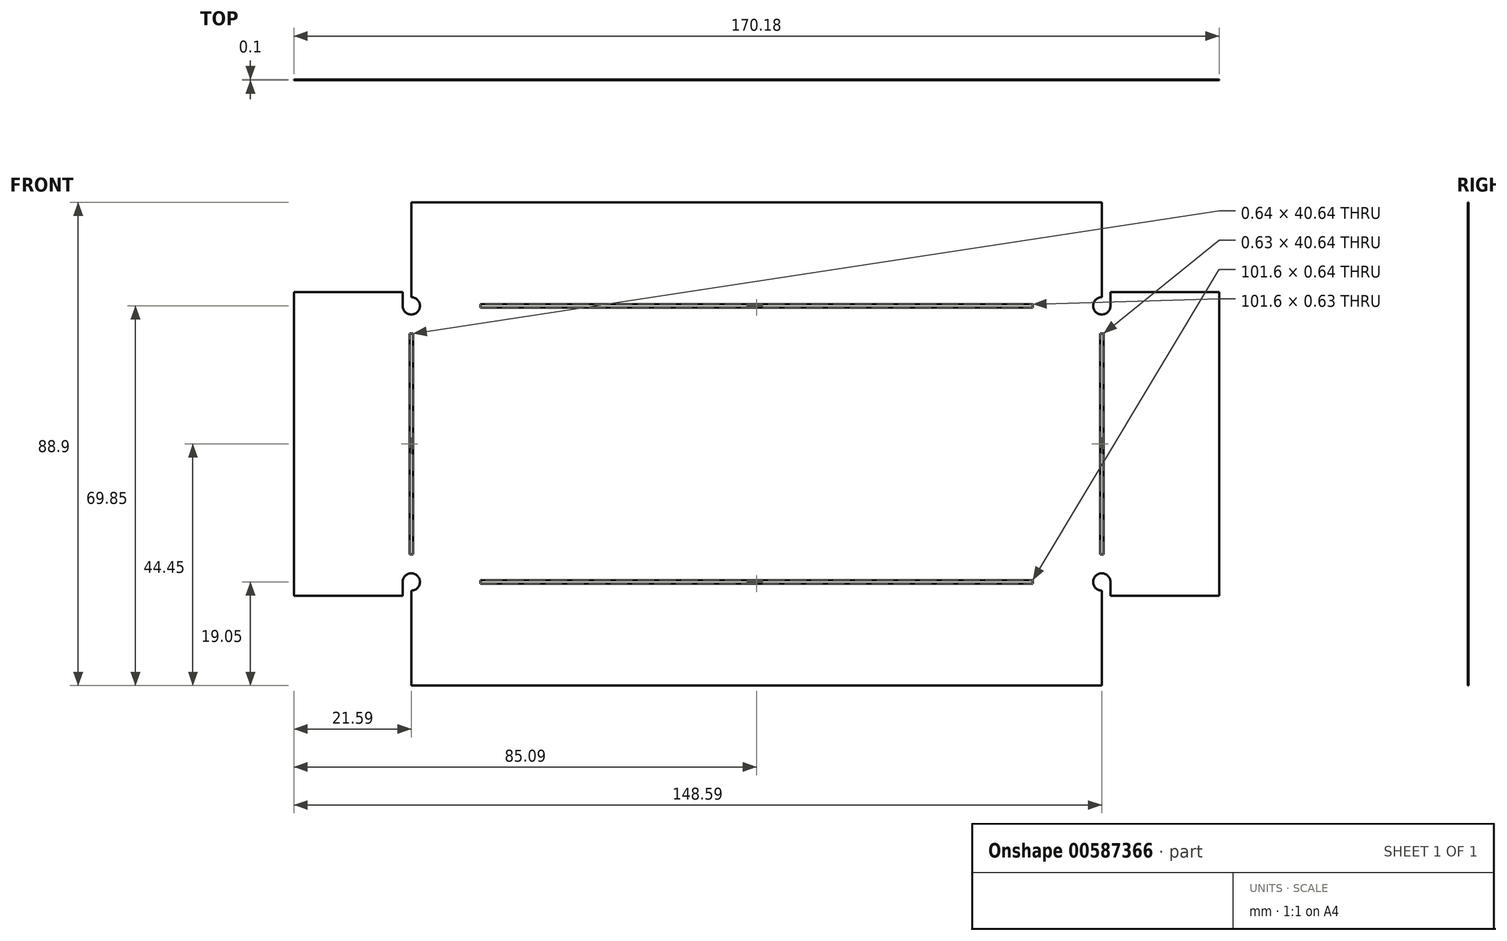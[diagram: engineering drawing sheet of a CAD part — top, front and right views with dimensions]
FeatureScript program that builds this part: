
annotation { "Feature Type Name" : "Feature", "Feature Type Description" : "" }
export const myFeature = defineFeature(function(context is Context, id is Id, definition is map)
    precondition{}
    {
        {
            assignVariable(context, id + "F0", {"name" : "matthick", "anyValue" : .1});
        }
        {
            var Q0;
            Q0=qCreatedBy(makeId("Front.planeOp"),FACE);
            var sketch = newSketch(context, id + "F1", { "sketchPlane" : qUnion([Q0])});
            skLineSegment(sketch, "E0.bottom", {"start": v(0, 0) * mm, "end": v(127, 0) * mm});
            skLineSegment(sketch, "E0.top", {"start": v(0, 50.8) * mm, "end": v(127, 50.8) * mm});
            skLineSegment(sketch, "E0.left", {"start": v(0, 0) * mm, "end": v(0, 50.8) * mm});
            skLineSegment(sketch, "E0.right", {"start": v(127, 0) * mm, "end": v(127, 50.8) * mm});
            skCircle(sketch, "E1", {"center": v(0, 50.8) * mm, "radius": 1.59 * mm});
            skLineSegment(sketch, "E2", {"start": v(63.5, 50.8) * mm, "end": v(63.5, 0) * mm, "construction": true});
            skLineSegment(sketch, "E3", {"start": v(0, 25.4) * mm, "end": v(127, 25.4) * mm, "construction": true});
            skCircle(sketch, "E4.MirrorC", {"center": v(127, 50.8) * mm, "radius": 1.59 * mm});
            skCircle(sketch, "E5.MirrorC", {"center": v(0, 0) * mm, "radius": 1.59 * mm});
            skCircle(sketch, "E6.MirrorC", {"center": v(127, 0) * mm, "radius": 1.59 * mm});
            skLineSegment(sketch, "E7", {"start": v(127, 50.8) * mm, "end": v(148.59, 50.8) * mm});
            skLineSegment(sketch, "E8", {"start": v(148.6, 50.8) * mm, "end": v(148.6, 0) * mm});
            skLineSegment(sketch, "E9", {"start": v(148.59, 0) * mm, "end": v(127, 0) * mm});
            skLineSegment(sketch, "E10", {"start": v(148.59, 50.8) * mm, "end": v(148.59, 53.34) * mm});
            skLineSegment(sketch, "E11", {"start": v(148.59, 53.34) * mm, "end": v(127, 53.34) * mm});
            skLineSegment(sketch, "E12", {"start": v(127, 50.8) * mm, "end": v(127, 53.34) * mm});
            skLineSegment(sketch, "E13.MirrorCS", {"start": v(148.59, -2.54) * mm, "end": v(127, -2.54) * mm});
            skLineSegment(sketch, "E14.MirrorCS", {"start": v(148.59, 0) * mm, "end": v(148.59, -2.54) * mm});
            skLineSegment(sketch, "E15.MirrorCS", {"start": v(127, 0) * mm, "end": v(127, -2.54) * mm});
            skLineSegment(sketch, "E16.MirrorCS", {"start": v(-21.6, -2.54) * mm, "end": v(0, -2.54) * mm});
            skLineSegment(sketch, "E17.MirrorCS", {"start": v(-21.6, 0) * mm, "end": v(-21.6, -2.54) * mm});
            skLineSegment(sketch, "E18.MirrorCS", {"start": v(-21.6, 0) * mm, "end": v(0, 0) * mm});
            skLineSegment(sketch, "E19.MirrorCS", {"start": v(0, 0) * mm, "end": v(0, -2.54) * mm});
            skLineSegment(sketch, "E20.MirrorCS", {"start": v(-21.6, 50.8) * mm, "end": v(-21.6, 0) * mm});
            skLineSegment(sketch, "E21.MirrorCS", {"start": v(0, 50.8) * mm, "end": v(-21.6, 50.8) * mm});
            skLineSegment(sketch, "E22.MirrorCS", {"start": v(-21.6, 53.34) * mm, "end": v(0, 53.34) * mm});
            skLineSegment(sketch, "E23.MirrorCS", {"start": v(-21.6, 50.8) * mm, "end": v(-21.6, 53.34) * mm});
            skLineSegment(sketch, "E24.MirrorCS", {"start": v(0, 50.8) * mm, "end": v(0, 53.34) * mm});
            skLineSegment(sketch, "E25", {"start": v(0, 50.8) * mm, "end": v(0, 69.85) * mm});
            skLineSegment(sketch, "E26", {"start": v(0, 69.85) * mm, "end": v(127, 69.85) * mm});
            skLineSegment(sketch, "E27", {"start": v(127, 69.85) * mm, "end": v(127, 50.8) * mm});
            skLineSegment(sketch, "E28.bottom", {"start": v(12.7, 51.12) * mm, "end": v(114.3, 51.12) * mm});
            skLineSegment(sketch, "E28.top", {"start": v(12.7, 50.48) * mm, "end": v(114.3, 50.48) * mm});
            skLineSegment(sketch, "E28.left", {"start": v(12.7, 51.12) * mm, "end": v(12.7, 50.48) * mm});
            skLineSegment(sketch, "E28.right", {"start": v(114.3, 51.12) * mm, "end": v(114.3, 50.48) * mm});
            skPoint(sketch, "E28.middle", {"position": v(63.5, 50.8) * mm});
            skLineSegment(sketch, "E29.MirrorCS", {"start": v(0, 0) * mm, "end": v(0, -19.05) * mm});
            skLineSegment(sketch, "E30.MirrorCS", {"start": v(0, -19.05) * mm, "end": v(127, -19.05) * mm});
            skLineSegment(sketch, "E31.MirrorCS", {"start": v(127, -19.05) * mm, "end": v(127, 0) * mm});
            skLineSegment(sketch, "E32.MirrorCS", {"start": v(114.3, -0.32) * mm, "end": v(114.3, 0.32) * mm});
            skLineSegment(sketch, "E33.MirrorCS", {"start": v(12.7, 0.32) * mm, "end": v(114.3, 0.32) * mm});
            skLineSegment(sketch, "E34.MirrorCS", {"start": v(12.7, -0.32) * mm, "end": v(114.3, -0.32) * mm});
            skLineSegment(sketch, "E35.MirrorCS", {"start": v(12.7, -0.32) * mm, "end": v(12.7, 0.32) * mm});
            skLineSegment(sketch, "E36", {"start": v(-1.59, 50.8) * mm, "end": v(-1.59, 53.34) * mm});
            skLineSegment(sketch, "E37", {"start": v(-1.59, 0) * mm, "end": v(-1.59, -2.54) * mm});
            skLineSegment(sketch, "E38.MirrorCS", {"start": v(128.59, 0) * mm, "end": v(128.59, -2.54) * mm});
            skLineSegment(sketch, "E39.MirrorCS", {"start": v(128.59, 50.8) * mm, "end": v(128.59, 53.34) * mm});
            skLineSegment(sketch, "E40.bottom", {"start": v(0.32, 45.72) * mm, "end": v(-0.32, 45.72) * mm});
            skLineSegment(sketch, "E40.top", {"start": v(0.32, 5.08) * mm, "end": v(-0.32, 5.08) * mm});
            skLineSegment(sketch, "E40.left", {"start": v(0.32, 45.72) * mm, "end": v(0.32, 5.08) * mm});
            skLineSegment(sketch, "E40.right", {"start": v(-0.32, 45.72) * mm, "end": v(-0.32, 5.08) * mm});
            skPoint(sketch, "E40.middle", {"position": v(0, 25.4) * mm});
            skLineSegment(sketch, "E41.MirrorCS", {"start": v(126.68, 45.72) * mm, "end": v(126.68, 5.08) * mm});
            skLineSegment(sketch, "E42.MirrorCS", {"start": v(127.32, 45.72) * mm, "end": v(127.32, 5.08) * mm});
            skLineSegment(sketch, "E43.MirrorCS", {"start": v(126.68, 45.72) * mm, "end": v(127.32, 45.72) * mm});
            skLineSegment(sketch, "E44.MirrorCS", {"start": v(126.68, 5.08) * mm, "end": v(127.32, 5.08) * mm});
            skSolve(sketch);
        }
        {
            var Q0;
            {var subQ0=sQuery(id+"F1.wireOp",EDGE,"E17.MirrorCS");Q0=makeQuery(id+"F1.imprint","IMPRINT",FACE,{"disambiguationData":[TD([[makeQuery(id+"F1.imprint","IMPRINT",EDGE,{"derivedFrom":subQ0}),1.0]])]});}
            var Q1;
            {var subQ0=sQuery(id+"F1.wireOp",EDGE,"E23.MirrorCS");Q1=makeQuery(id+"F1.imprint","IMPRINT",FACE,{"disambiguationData":[TD([[makeQuery(id+"F1.imprint","IMPRINT",EDGE,{"derivedFrom":subQ0}),-1.0]])]});}
            var Q2;
            {var subQ0=sQuery(id+"F1.wireOp",EDGE,"E10");Q2=makeQuery(id+"F1.imprint","IMPRINT",FACE,{"disambiguationData":[TD([[makeQuery(id+"F1.imprint","IMPRINT",EDGE,{"derivedFrom":subQ0}),1.0]])]});}
            var Q3;
            {var subQ0=sQuery(id+"F1.wireOp",EDGE,"E14.MirrorCS");Q3=makeQuery(id+"F1.imprint","IMPRINT",FACE,{"disambiguationData":[TD([[makeQuery(id+"F1.imprint","IMPRINT",EDGE,{"derivedFrom":subQ0}),-1.0]])]});}
            var Q4;
            {var subQ5=sQuery(id+"F1.wireOp",EDGE,"E20.MirrorCS");Q4=makeQuery(id+"F1.imprint","IMPRINT",FACE,{"disambiguationData":[TD([[makeQuery(id+"F1.imprint","IMPRINT",EDGE,{"derivedFrom":subQ5}),1.0]])]});}
            var Q5;
            {var subQ12=sQuery(id+"F1.wireOp",EDGE,"E8");Q5=makeQuery(id+"F1.imprint","IMPRINT",FACE,{"disambiguationData":[TD([[makeQuery(id+"F1.imprint","IMPRINT",EDGE,{"derivedFrom":subQ12}),-1.0]])]});}
            var Q6;
            {var subQ2=sQuery(id+"F1.wireOp",EDGE,"E30.MirrorCS");Q6=makeQuery(id+"F1.imprint","IMPRINT",FACE,{"disambiguationData":[TD([[makeQuery(id+"F1.imprint","IMPRINT",EDGE,{"derivedFrom":subQ2}),1.0]])]});}
            var Q7;
            {var subQ3=sQuery(id+"F1.wireOp",EDGE,"E26");Q7=makeQuery(id+"F1.imprint","IMPRINT",FACE,{"disambiguationData":[TD([[makeQuery(id+"F1.imprint","IMPRINT",EDGE,{"derivedFrom":subQ3}),-1.0]])]});}
            var Q8;
            {var subQ14=sQuery(id+"F1.wireOp",EDGE,"E28.top");Q8=makeQuery(id+"F1.imprint","IMPRINT",FACE,{"disambiguationData":[TD([[makeQuery(id+"F1.imprint","IMPRINT",EDGE,{"derivedFrom":subQ14}),-1.0]])]});}
            extrude(context, id + "F2", {"entities" : qUnion([Q0, Q1, Q2, Q3, Q4, Q5, Q6, Q7, Q8]), "depth" : (getVariable(context, 'matthick')) * mm, "offsetDistance" : 25.4 * mm});
        }
    });
